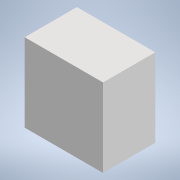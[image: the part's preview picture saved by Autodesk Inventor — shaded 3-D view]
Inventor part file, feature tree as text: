
AUTODESK INVENTOR PART (.ipt)
format: ipt  version: 2022 (Build 260153000, 153)  size: 174,080 bytes
history: native  units: in
note: dims shown in document units (in); Inventor stores cm internally (conversion verified against a paired STEP export)
features: extrude x2, sketch x2, projected_geometry x1
ambient origin geometry x8: Origin, YZ Plane, XZ Plane, XY Plane, X Axis, Y Axis, Z Axis, Center Point
bodies: Solid1 (feature_tree)
feature tree (5):
  extrude  "Extrusion1"  Depth=3.0in
  extrude  "Extrusion2"  Depth=0.78in
  sketch  "Sketch1"  dims[d0=3.0in d1=3.0in]
  sketch  "Sketch2"  dims[d2=2.76in d3=0.78in d4=0.78in d5=1.1811in d7=1.0in d8=0.3937in d10=1.0in d12=1.1811in d14=1.0in d15=0.3937in d17=1.0in d19=0.42in d20=0.0in d21=1.58in d22=0.0in]
  projected_geometry  "Projected Loop1"
